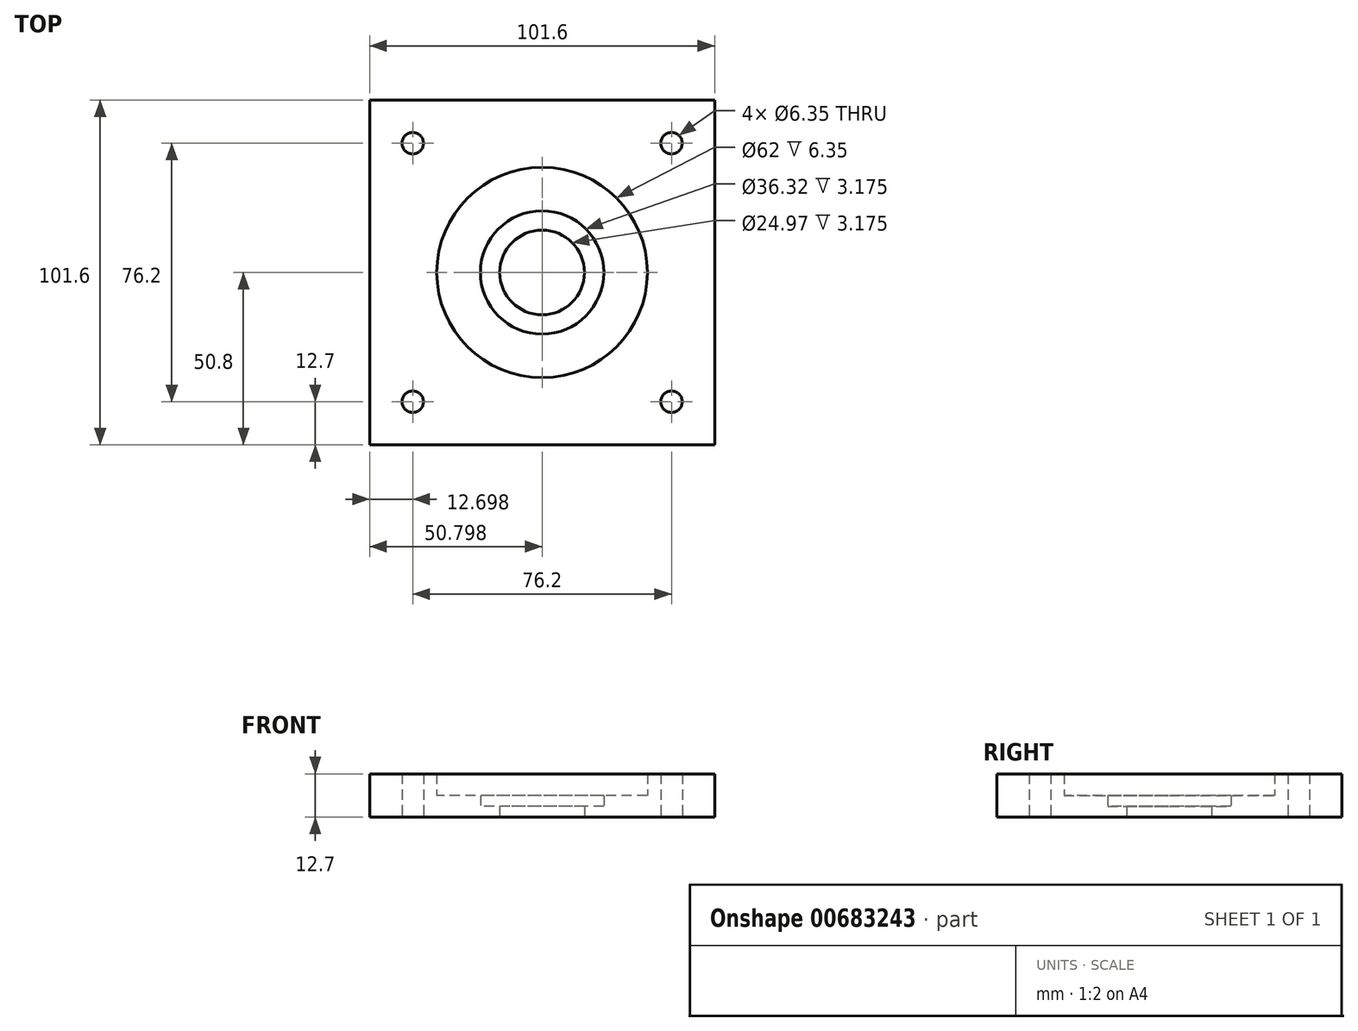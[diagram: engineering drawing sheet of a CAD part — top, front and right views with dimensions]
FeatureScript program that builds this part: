
annotation { "Feature Type Name" : "Feature", "Feature Type Description" : "" }
export const myFeature = defineFeature(function(context is Context, id is Id, definition is map)
    precondition{}
    {
        {
            var Q0;
            Q0=qCreatedBy(makeId("Top.planeOp"),FACE);
            var sketch = newSketch(context, id + "F0", { "sketchPlane" : qUnion([Q0])});
            skLineSegment(sketch, "E0", {"start": v(-41.05, 0) * mm, "end": v(-41.05, -50.82) * mm});
            skLineSegment(sketch, "E1", {"start": v(-41.05, -50.82) * mm, "end": v(60.55, -50.82) * mm});
            skLineSegment(sketch, "E2", {"start": v(60.55, -50.82) * mm, "end": v(60.55, 50.78) * mm});
            skLineSegment(sketch, "E3", {"start": v(60.55, 50.78) * mm, "end": v(-41.05, 50.78) * mm});
            skLineSegment(sketch, "E4", {"start": v(-41.05, 50.78) * mm, "end": v(-41.05, 0) * mm});
            skCircle(sketch, "E5", {"center": v(9.75, -0.02) * mm, "radius": 31 * mm});
            skPoint(sketch, "E5.centerSnap0", {"position": v(60.55, -0.02) * mm});
            skPoint(sketch, "E5.centerSnap1", {"position": v(9.75, 50.78) * mm});
            skCircle(sketch, "E6", {"center": v(9.75, -0.02) * mm, "radius": 12.48 * mm});
            skCircle(sketch, "E7", {"center": v(9.75, -0.02) * mm, "radius": 18.16 * mm});
            skCircle(sketch, "E8", {"center": v(-28.35, 38.08) * mm, "radius": 3.18 * mm});
            skCircle(sketch, "E9.0.1.0", {"center": v(-28.35, -38.12) * mm, "radius": 3.18 * mm});
            skCircle(sketch, "E9.1.0.0", {"center": v(47.85, 38.08) * mm, "radius": 3.18 * mm});
            skCircle(sketch, "E9.1.1.0", {"center": v(47.85, -38.12) * mm, "radius": 3.18 * mm});
            skLineSegment(sketch, "E9.direction1", {"start": v(-28.35, 38.08) * mm, "end": v(47.85, 38.08) * mm, "construction": true});
            skLineSegment(sketch, "E9.direction2", {"start": v(-28.35, 38.08) * mm, "end": v(-28.35, -38.12) * mm, "construction": true});
            skSolve(sketch);
        }
        {
            var Q0;
            Q0=makeQuery(id+"F0.imprint","IMPRINT",FACE,{"disambiguationData":[TD([[makeQuery(id+"F0.imprint","IMPRINT",EDGE,{"derivedFrom":sQuery(id+"F0.wireOp",EDGE,"E0")}),1.0]])]});
            extrude(context, id + "F1", {"entities" : qUnion([Q0]), "depth" : 12.7 * mm, "offsetDistance" : 25.4 * mm});
        }
        {
            var Q0;
            Q0=makeQuery(id+"F0.imprint","IMPRINT",FACE,{"disambiguationData":[TD([[makeQuery(id+"F0.imprint","IMPRINT",EDGE,{"derivedFrom":sQuery(id+"F0.wireOp",EDGE,"E5")}),1.0]])]});
            extrude(context, id + "F2", {"entities" : qUnion([Q0]), "operationType" : NewBodyOperationType.ADD, "depth" : 6.35 * mm, "offsetDistance" : 25.4 * mm});
        }
        {
            var Q0;
            Q0=makeQuery(id+"F0.imprint","IMPRINT",FACE,{"disambiguationData":[TD([[makeQuery(id+"F0.imprint","IMPRINT",EDGE,{"derivedFrom":sQuery(id+"F0.wireOp",EDGE,"E6")}),-1.0]])]});
            extrude(context, id + "F3", {"entities" : qUnion([Q0]), "operationType" : NewBodyOperationType.ADD, "depth" : 3.17 * mm, "offsetDistance" : 25.4 * mm});
        }
    });
